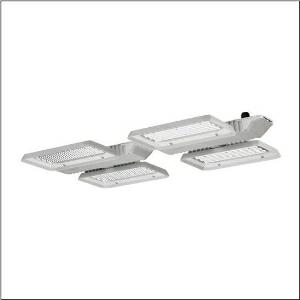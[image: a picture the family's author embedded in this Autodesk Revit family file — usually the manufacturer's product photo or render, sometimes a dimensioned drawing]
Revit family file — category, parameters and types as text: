
# Revit family: highbay_21_51hla2d24mcb
name_source: partatom
category: Lighting Fixtures
units: mm (PartAtom-declared; Revit-internal decimal feet)

## family parameters
Cut with Voids When Loaded = No
Host = Face
Light Source = No
Part Type = Normal
Room Calculation Point = No
Round Connector Dimension = Use Diameter
Shared = No

## types (1)
- --- (1 x LED, 27600 lm, 171.1 W, 4000K)
    Apparent Load = 171 VA
    CIE Flux Codes = 89 96 99 100 100
    Color Rendering = 80
    Color Temperature = 4000K
    Default Elevation = 1800 mm
    Description = Highbay 21, LED high bay luminaire, primary light control with lens, of PMMA, light emission: direct distribution, primary light characteristic: symmetric, installation type: suspended mounting, surface-mounted, for 2x 2 x LED rated luminous flux: 27.600 lm, light colour: 840, colour temperature: 4000K, control gear: ECG DALI, with terminal, 5-pole, max. 2.5mm², mains connection: 230..240V, AC, 50/60Hz, rated input power: 171W, LED unit, of diecast aluminium, unplated, bead blasted, silver, length: 940 mm, width: 500 mm, height: 65mm, housing, of diecast aluminium, uncoated, bead blasted, silver, protection rating (complete): IP65, insulation class (complete): insulation class I (protective earthing), certification: CE, ENEC, VDE, protection symbol: D, impact resistance: IK08 with glass or PC cover, permissible ambient temperature for indoor applications: -35..+45°C, corresponds to IFS (International Featured Standards) requirements for safety and quality in the food industry, reducing of maximum allowable ambient temperature of 5°C with ceiling mounting, packaging unit: 1 piece
    Height = 95 mm
    Lamp = 1 x LED
    Lamp Light Flux = 27600 lm
    Lamp Power = 171.1 W
    Lamp count = 1
    Length = 939 mm
    Luminous efficacy = 161 lm/W
    Manufacturer = Siteco
    ModVariant = No
    Model = 51HLA2D24MCB
    Mounting Place = Ceiling
    Mounting Type = Pendant
    Number of Poles = 1
    OnlyDefault = Yes
    Power Factor = 1
    Product Name = Highbay 21
    Product group = LED high bay luminaire
    ProductGroupID = 903
    Protection Class = Protection class I
    Protection Degree = IP 65
    RLX_Detail_Level = 1
    RlxData = <blob elided: 64377 chars, md5=de8fbbf0>
    Socket = socket
    Standby Power = 0 W
    System Light Flux = 27600 lm
    System Power = 171 W
    Type Comments = factory setting: luminous flux: 100 % | dim-lin: 254 | 491 mA
    Type Image = l_1003428.jpg
    URL = http://relux.com
    VarID = @adj_135687
    Voltage = 0 V
    Weight = 0.00 kg
    Width = 501 mm

## geometry (parser evidence)
native form markers: Blend x4, Sweep x12
no freeform markers — native parametric forms only
